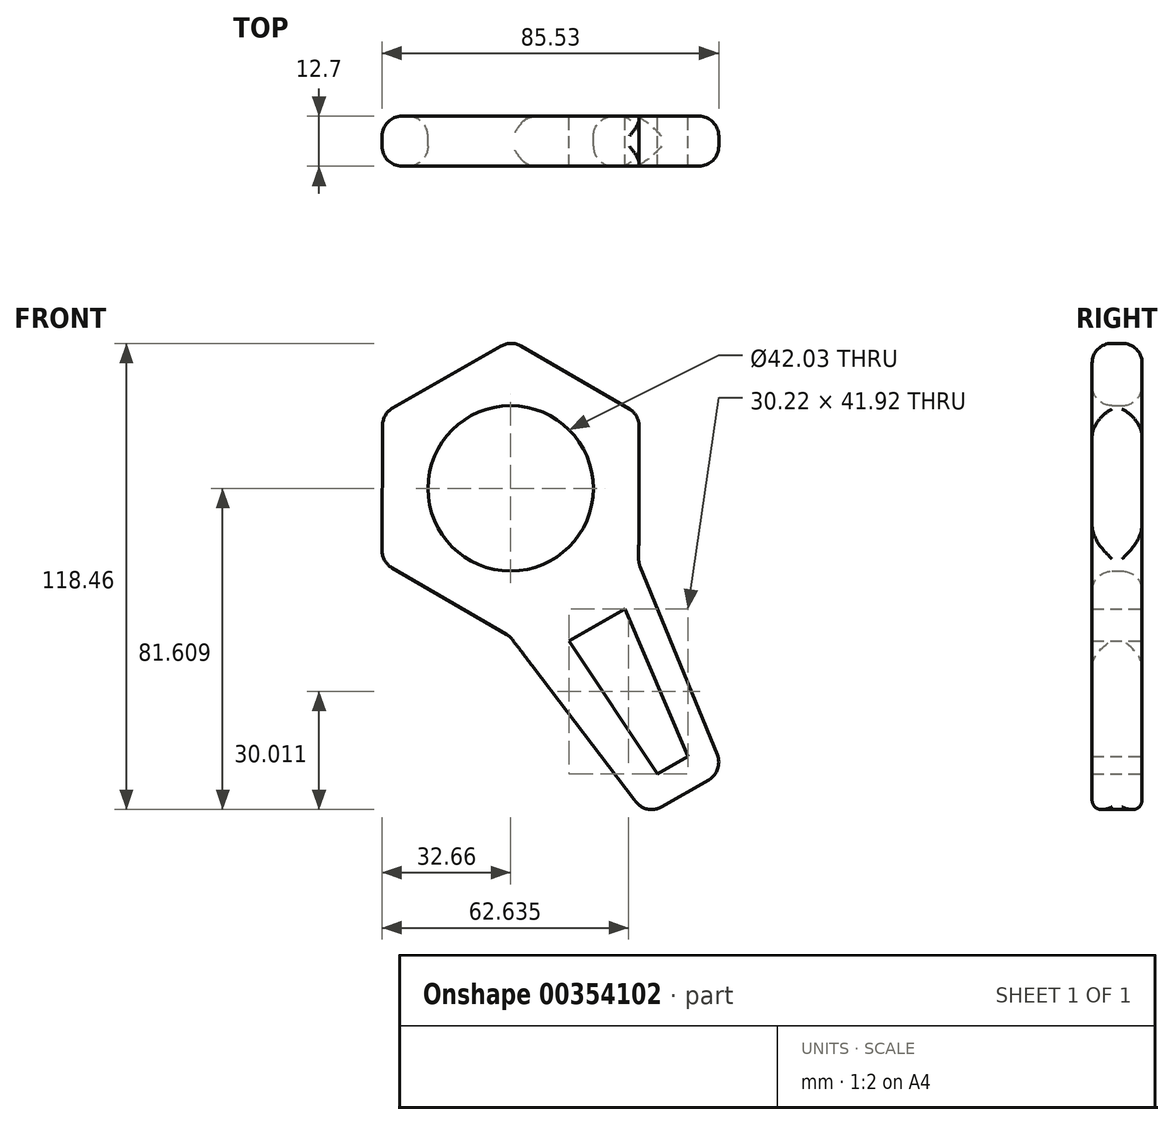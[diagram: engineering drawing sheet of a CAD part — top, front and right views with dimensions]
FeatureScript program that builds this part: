
annotation { "Feature Type Name" : "Feature", "Feature Type Description" : "" }
export const myFeature = defineFeature(function(context is Context, id is Id, definition is map)
    precondition{}
    {
        {
            var Q0;
            Q0=qCreatedBy(makeId("Front.planeOp"),FACE);
            var sketch = newSketch(context, id + "F0", { "sketchPlane" : qUnion([Q0])});
            skCircle(sketch, "E0.cCircle", {"center": v(-7.67, 13.4) * mm, "radius": 32.6 * mm, "construction": true});
            skLineSegment(sketch, "E0.0", {"start": v(24.85, -5.55) * mm, "end": v(-7.82, -24.23) * mm});
            skLineSegment(sketch, "E0.1", {"start": v(-7.82, -24.23) * mm, "end": v(-40.35, -5.28) * mm});
            skLineSegment(sketch, "E0.2", {"start": v(-40.35, -5.28) * mm, "end": v(-40.2, 32.36) * mm});
            skLineSegment(sketch, "E0.3", {"start": v(-40.2, 32.36) * mm, "end": v(-7.52, 51.05) * mm});
            skLineSegment(sketch, "E0.4", {"start": v(-7.52, 51.05) * mm, "end": v(25, 32.1) * mm});
            skLineSegment(sketch, "E0.5", {"start": v(25, 32.1) * mm, "end": v(24.85, -5.55) * mm});
            skPoint(sketch, "E0.0.midPoint", {"position": v(8.51, -14.89) * mm});
            skLineSegment(sketch, "E1", {"start": v(-7.82, -24.23) * mm, "end": v(26.82, -69.75) * mm});
            skLineSegment(sketch, "E2", {"start": v(24.85, -5.55) * mm, "end": v(46.5, -58.42) * mm});
            skLineSegment(sketch, "E3", {"start": v(26.82, -69.75) * mm, "end": v(46.5, -58.42) * mm});
            skCircle(sketch, "E4", {"center": v(-7.67, 13.4) * mm, "radius": 21.01 * mm});
            skLineSegment(sketch, "E5", {"start": v(7.2, -25.33) * mm, "end": v(21.36, -17.23) * mm});
            skLineSegment(sketch, "E6", {"start": v(21.36, -17.23) * mm, "end": v(37.41, -54.68) * mm});
            skLineSegment(sketch, "E7", {"start": v(37.41, -54.68) * mm, "end": v(29.6, -59.15) * mm});
            skLineSegment(sketch, "E8", {"start": v(29.6, -59.15) * mm, "end": v(7.2, -25.33) * mm});
            skSolve(sketch);
        }
        {
            var Q0;
            Q0=makeQuery(id+"F0.imprint","IMPRINT",FACE,{"disambiguationData":[TD([[makeQuery(id+"F0.imprint","IMPRINT",EDGE,{"derivedFrom":sQuery(id+"F0.wireOp",EDGE,"E0.0")}),-1.0]])]});
            var Q1;
            Q1=makeQuery(id+"F0.imprint","IMPRINT",FACE,{"disambiguationData":[TD([[makeQuery(id+"F0.imprint","IMPRINT",EDGE,{"derivedFrom":sQuery(id+"F0.wireOp",EDGE,"E0.0")}),1.0]])]});
            extrude(context, id + "F1", {"entities" : qUnion([Q0, Q1]), "depth" : 12.7 * mm});
        }
        {
            var Q0;
            Q0=makeQuery(id+"F1.opExtrude","CAP_EDGE",EDGE,{"disambiguationData":[OSD([sQuery(id+"F0.wireOp",EDGE,"E4")])],"isStart":false});
            var Q1;
            Q1=makeQuery(id+"F1.opExtrude","SWEPT_FACE",FACE,{"disambiguationData":[OSD([sQuery(id+"F0.wireOp",EDGE,"E0.1")])]});
            var Q2;
            Q2=makeQuery(id+"F1.opExtrude","SWEPT_FACE",FACE,{"disambiguationData":[OSD([sQuery(id+"F0.wireOp",EDGE,"E0.2")])]});
            var Q3;
            Q3=makeQuery(id+"F1.opExtrude","SWEPT_FACE",FACE,{"disambiguationData":[OSD([sQuery(id+"F0.wireOp",EDGE,"E3")])]});
            var Q4;
            Q4=makeQuery(id+"F1.opExtrude","SWEPT_FACE",FACE,{"disambiguationData":[OSD([sQuery(id+"F0.wireOp",EDGE,"E2")])]});
            var Q5;
            Q5=makeQuery(id+"F1.opExtrude","SWEPT_FACE",FACE,{"disambiguationData":[OSD([sQuery(id+"F0.wireOp",EDGE,"E0.4")])]});
            var Q6;
            Q6=makeQuery(id+"F1.opExtrude","SWEPT_FACE",FACE,{"disambiguationData":[OSD([sQuery(id+"F0.wireOp",EDGE,"E0.3")])]});
            var Q7;
            Q7=makeQuery(id+"F1.opExtrude","CAP_EDGE",EDGE,{"disambiguationData":[OSD([sQuery(id+"F0.wireOp",EDGE,"E4")])],"isStart":true});
            fillet(context, id + "F2", {"entities" : qUnion([Q0, Q1, Q2, Q3, Q4, Q5, Q6, Q7]), "radius" : 5.08 * mm, "tangentPropagation" : true, "allowEdgeOverflow" : false});
        }
    });
